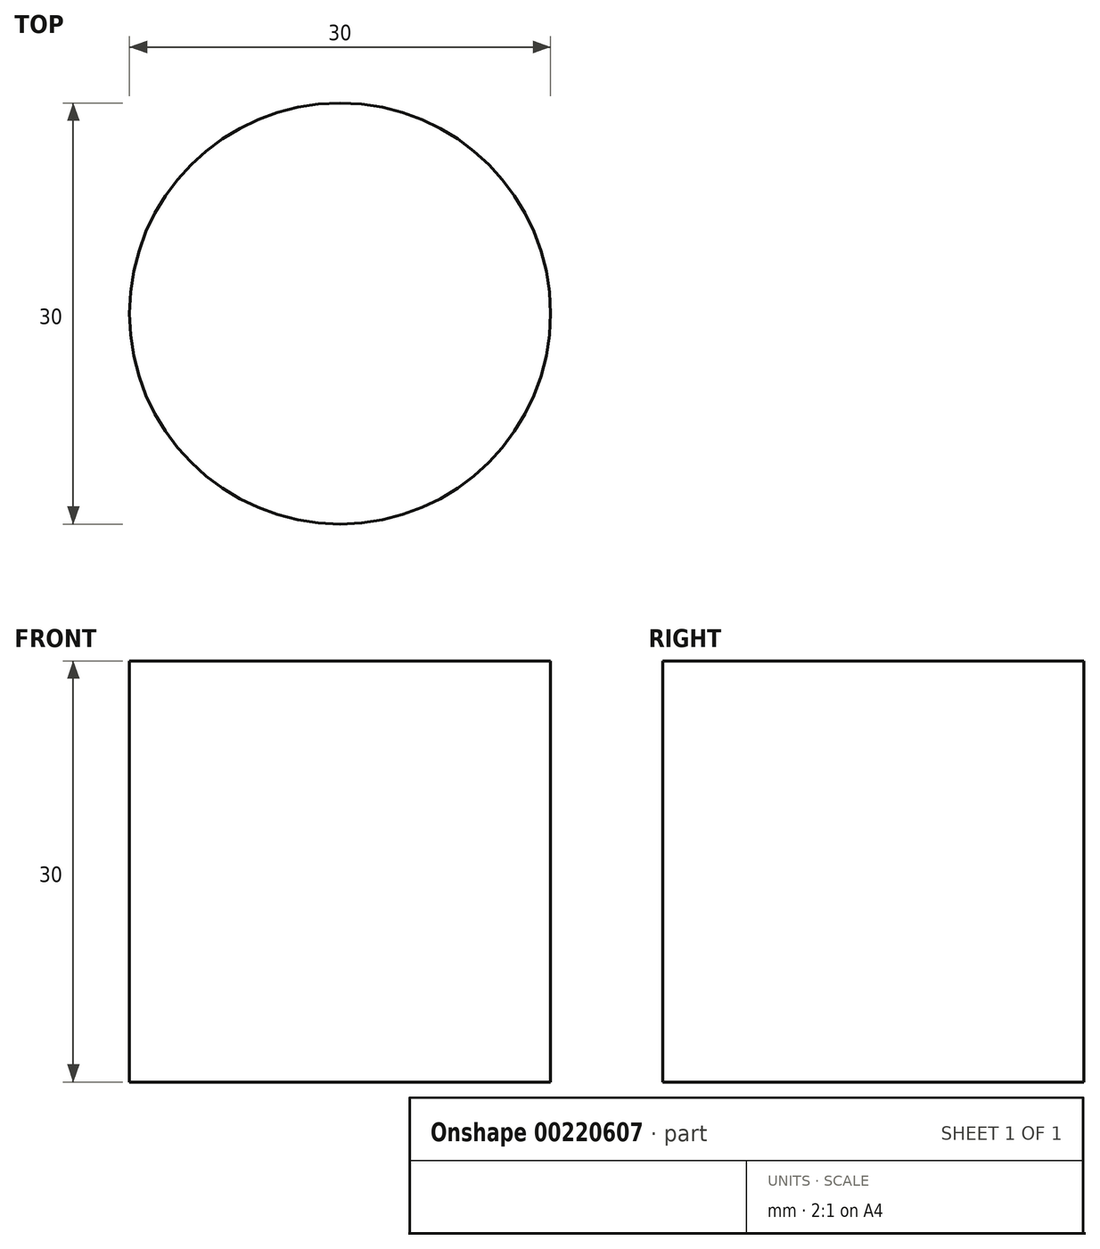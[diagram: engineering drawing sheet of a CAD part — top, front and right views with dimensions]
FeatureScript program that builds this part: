
annotation { "Feature Type Name" : "Feature", "Feature Type Description" : "" }
export const myFeature = defineFeature(function(context is Context, id is Id, definition is map)
    precondition{}
    {
        {
            var Q0;
            Q0=qCreatedBy(makeId("Top.planeOp"),FACE);
            var sketch = newSketch(context, id + "F0", { "sketchPlane" : qUnion([Q0])});
            skEllipse(sketch, "E0", {"center": v(0, 0) * mm, "majorRadius": 15 * mm, "minorRadius": 15 * mm, "majorAxis": v(0, 1)});
            skSolve(sketch);
        }
        {
            var Q0;
            Q0 = qSketchRegion(id + "F0", true);
            extrude(context, id + "F1", {"entities" : qUnion([Q0]), "depth" : 30 * mm});
        }
    });
